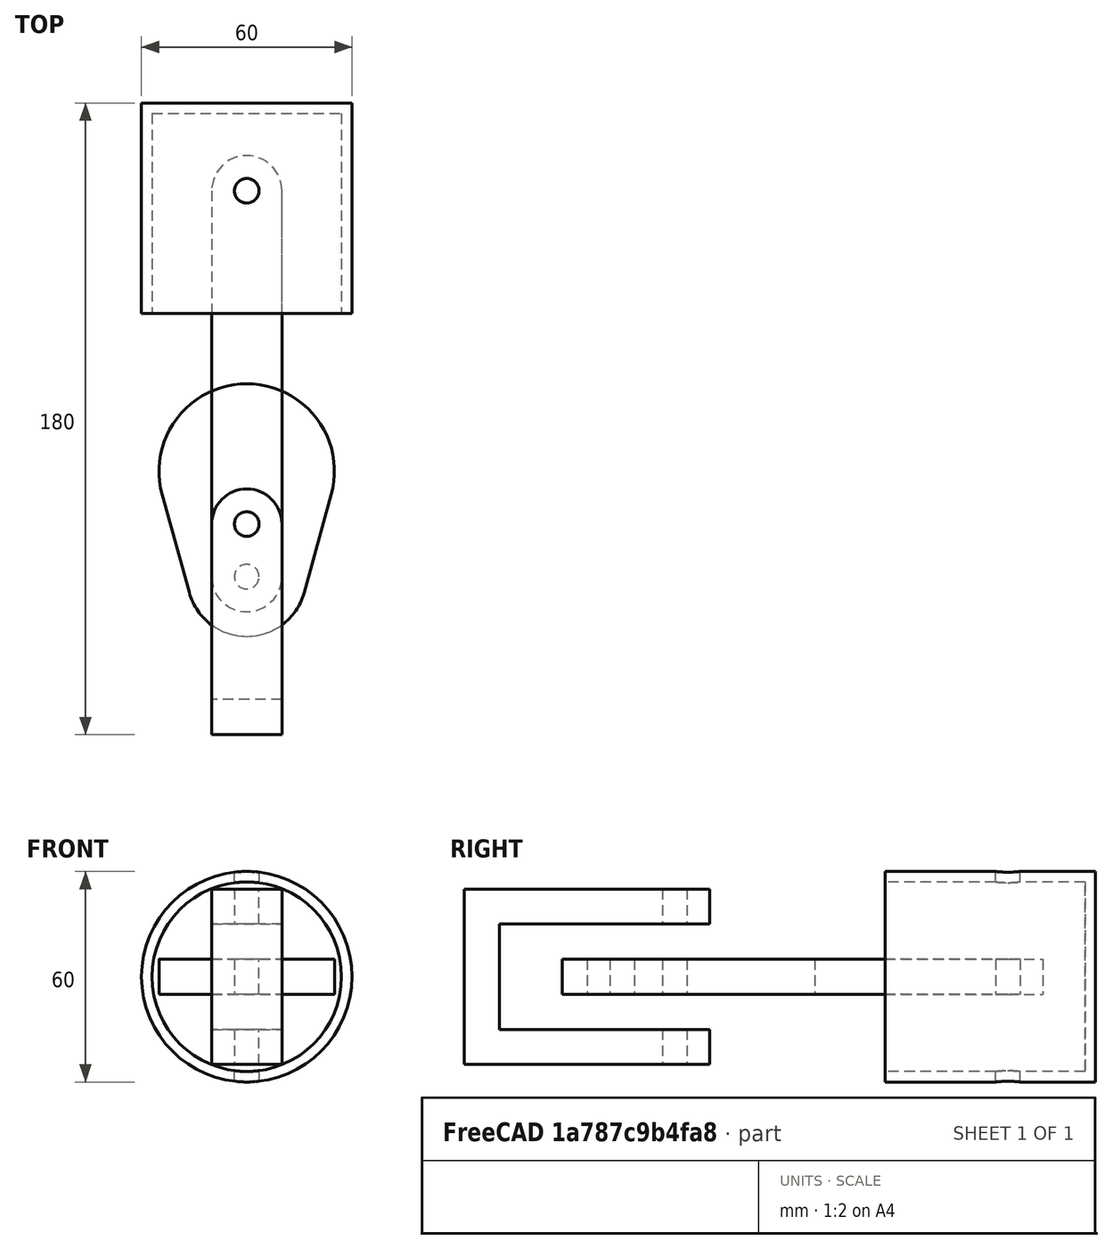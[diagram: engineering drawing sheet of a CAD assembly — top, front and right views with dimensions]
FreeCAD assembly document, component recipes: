
FREECAD ASSEMBLY — COMPONENT RECIPES ("Piston Head Assembly")

This assembly document has 5 components, labeled P0..P4 below (a component is one placed body or linked part). 5 of them carry a construction recipe — the FreeCAD feature program that regenerates the part from scratch, quoted from this document or its linked companion documents; the rest are supplied as boundary geometry only. No exploded tour is included for this assembly.
COMPONENT P0 — recipe-attached ("Crank001", modeled in this document).
Construction recipe (the document's own serialized feature program — sketch geometry with constraints, then the solid features built on it; lengths are millimeters unless a unit is written):

FEATURE [PartDesign::SubShapeBinder] Binder002
  BindCopyOnChange = 0
  BindMode = 0
  ClaimChildren = false
  Context = -> Body002 [Binder002.]
  Fuse = false
  MakeFace = false
  OffsetFill = false
  OffsetIntersection = false
  OffsetJoinType = 0
  OffsetOpenResult = false
  PartialLoad = false
  Refine = true
  Relative = true
  Support = -> [Sketch]
  _Version = 2
FEATURE [Sketcher::SketchObject] Sketch003
  ArcFitTolerance = 1e-06
  AttachmentSupport = -> [XY_Plane002]
  ExternalGeometry = -> [Binder002]
  FullyConstrained = true
  MakeInternals = false
  MapMode = 5
  sketch-geometry (6):
    g0: LineSegment StartX=-24.0947 StartY=-31.6667 StartZ=0 EndX=-16.3844 EndY=-59.5333 EndZ=0
    g1: ArcOfCircle CenterX=0 CenterY=-55 CenterZ=0 NormalX=0 NormalY=0 NormalZ=1 AngleXU=0 Radius=17 StartAngle=3.41153 EndAngle=6.01325
    g2: LineSegment StartX=16.3844 StartY=-59.5333 StartZ=0 EndX=24.0947 EndY=-31.6667 EndZ=0
    g3: ArcOfCircle CenterX=-1.6e-15 CenterY=-25 CenterZ=0 NormalX=0 NormalY=0 NormalZ=1 AngleXU=0 Radius=25 StartAngle=6.01325 EndAngle=9.69471
    g4: Circle CenterX=0 CenterY=-40 CenterZ=0 NormalX=0 NormalY=0 NormalZ=1 AngleXU=0 Radius=3.5
    g5: Circle CenterX=0 CenterY=-55 CenterZ=0 NormalX=0 NormalY=0 NormalZ=1 AngleXU=0 Radius=3.5
  constraints (12):
    c: Coincident(g-4,g0)
    c: Tangent(g0,g1) = -1.5708
    c: Coincident(g1,g-6)
    c: Coincident(g1,g2)
    c: Coincident(g2,g-6)
    c: Tangent(g2,g3) = -1.5708
    c: Coincident(g3,g0)
    c: Coincident(g0,g-5)
    c: Coincident(g4,g-7)
    c: Equal(g4,g-7)
    c: Coincident(g5,g1)
    c: Equal(g5,g-8)
FEATURE [PartDesign::Pad] Pad001
  Direction = (0,0,1)
  Length = 10
  Length2 = 10
  Midplane = true
  Profile = -> Sketch003
  ReferenceAxis = -> Sketch003 [N_Axis]
  Refine = true
  Suppressed = false
  Type = 0
FEATURE [PartDesign::Body] Body002  label="Crank"
  AllowCompound = false
  Group = -> [Binder002,Sketch003,Pad001]
  Origin = -> Origin002
  Tip = -> Pad001
COMPONENT P1 — same part as P0; its construction recipe is shown at P0.
COMPONENT P2 — recipe-attached ("Link001", modeled in this document).
Construction recipe (the document's own serialized feature program — sketch geometry with constraints, then the solid features built on it; lengths are millimeters unless a unit is written):

FEATURE [PartDesign::SubShapeBinder] Binder
  BindCopyOnChange = 0
  BindMode = 0
  ClaimChildren = false
  Context = -> Body [Binder.]
  Fuse = false
  MakeFace = false
  OffsetFill = false
  OffsetIntersection = false
  OffsetJoinType = 0
  OffsetOpenResult = false
  PartialLoad = false
  Refine = true
  Relative = true
  Support = -> [Sketch]
  _Version = 2
FEATURE [Sketcher::SketchObject] Sketch001
  ArcFitTolerance = 1e-06
  AttachmentSupport = -> [XY_Plane]
  ExternalGeometry = -> [Binder]
  FullyConstrained = true
  MakeInternals = false
  MapMode = 5
  sketch-geometry (6):
    g0: LineSegment StartX=-10 StartY=55 StartZ=0 EndX=-10 EndY=-55 EndZ=0
    g1: ArcOfCircle CenterX=3e-16 CenterY=-55 CenterZ=0 NormalX=0 NormalY=0 NormalZ=1 AngleXU=0 Radius=10 StartAngle=3.14159 EndAngle=6.28319
    g2: LineSegment StartX=10 StartY=-55 StartZ=0 EndX=10 EndY=55 EndZ=0
    g3: ArcOfCircle CenterX=-4e-16 CenterY=55 CenterZ=0 NormalX=0 NormalY=0 NormalZ=1 AngleXU=0 Radius=10 StartAngle=0 EndAngle=3.14159
    g4: Circle CenterX=3e-16 CenterY=-55 CenterZ=0 NormalX=0 NormalY=0 NormalZ=1 AngleXU=0 Radius=3.5
    g5: Circle CenterX=-4e-16 CenterY=55 CenterZ=0 NormalX=0 NormalY=0 NormalZ=1 AngleXU=0 Radius=3.5
  constraints (12):
    c: Coincident(g-4,g0)
    c: Coincident(g0,g-6)
    c: Tangent(g0,g1) = -1.5708
    c: Coincident(g1,g-6)
    c: Coincident(g1,g2)
    c: Coincident(g2,g-5)
    c: Tangent(g2,g3) = -1.5708
    c: Coincident(g3,g0)
    c: Coincident(g4,g1)
    c: Equal(g4,g-7)
    c: Coincident(g5,g3)
    c: Equal(g5,g-8)
FEATURE [PartDesign::Pad] Pad
  Direction = (0,0,1)
  Length = 10
  Length2 = 10
  Midplane = true
  Profile = -> Sketch001
  ReferenceAxis = -> Sketch001 [N_Axis]
  Refine = true
  Suppressed = false
  Type = 0
FEATURE [PartDesign::Body] Body  label="Link"
  AllowCompound = false
  Group = -> [Binder,Sketch001,Pad]
  Origin = -> Origin
  Tip = -> Pad
COMPONENT P3 — recipe-attached ("Mount001", modeled in this document).
Construction recipe (the document's own serialized feature program — sketch geometry with constraints, then the solid features built on it; lengths are millimeters unless a unit is written):

FEATURE [PartDesign::SubShapeBinder] Binder003
  BindCopyOnChange = 0
  BindMode = 0
  ClaimChildren = false
  Context = -> Body003 [Binder003.]
  Fuse = false
  MakeFace = false
  OffsetFill = false
  OffsetIntersection = false
  OffsetJoinType = 0
  OffsetOpenResult = false
  PartialLoad = false
  Refine = true
  Relative = true
  Support = -> [Sketch]
  _Version = 2
FEATURE [Sketcher::SketchObject] Sketch005
  ArcFitTolerance = 1e-06
  AttachmentSupport = -> [XY_Plane003]
  ExternalGeometry = -> [Binder003]
  FullyConstrained = true
  MakeInternals = false
  MapMode = 5
  sketch-geometry (5):
    g0: LineSegment StartX=-10 StartY=-40 StartZ=0 EndX=-10 EndY=-100 EndZ=0
    g1: LineSegment StartX=-10 StartY=-100 StartZ=0 EndX=10 EndY=-100 EndZ=0
    g2: LineSegment StartX=10 StartY=-100 StartZ=0 EndX=10 EndY=-40 EndZ=0
    g3: ArcOfCircle CenterX=1.8e-15 CenterY=-40 CenterZ=0 NormalX=0 NormalY=0 NormalZ=1 AngleXU=0 Radius=10 StartAngle=1e-16 EndAngle=3.14159
    g4: Circle CenterX=1.8e-15 CenterY=-40 CenterZ=0 NormalX=0 NormalY=0 NormalZ=1 AngleXU=0 Radius=3.5
  constraints (10):
    c: Tangent(g-4,g0) = -1.5708
    c: Coincident(g0,g1)
    c: Coincident(g1,g-6)
    c: Horizontal(g1)
    c: Coincident(g1,g2)
    c: Coincident(g2,g-5)
    c: Tangent(g2,g3) = -1.5708
    c: Coincident(g3,g0)
    c: Coincident(g4,g3)
    c: Equal(g4,g-7)
FEATURE [PartDesign::Pad] Pad002
  Direction = (0,0,1)
  Length = 50
  Length2 = 10
  Midplane = true
  Profile = -> Sketch005
  ReferenceAxis = -> Sketch005 [N_Axis]
  Refine = true
  Suppressed = false
  Type = 0
FEATURE [Sketcher::SketchObject] Sketch006
  ArcFitTolerance = 1e-06
  AttachmentSupport = -> [YZ_Plane003]
  ExternalGeometry = -> [Pad002]
  FullyConstrained = false
  MakeInternals = false
  MapMode = 5
  Placement = pos=(0,0,0) rot=(0.57735,0.57735,0.57735;2.0944rad)
  sketch-geometry (4):
    g0: LineSegment StartX=-90 StartY=15 StartZ=0 EndX=-90 EndY=-15 EndZ=0
    g1: LineSegment StartX=-90 StartY=-15 StartZ=0 EndX=-12.8642 EndY=-15 EndZ=0
    g2: LineSegment StartX=-12.8642 StartY=-15 StartZ=0 EndX=-12.8642 EndY=15 EndZ=0
    g3: LineSegment StartX=-12.8642 StartY=15 StartZ=0 EndX=-90 EndY=15 EndZ=0
  constraints (10):
    c: Coincident(g0,g1)
    c: Coincident(g1,g2)
    c: Coincident(g2,g3)
    c: Coincident(g3,g0)
    c: Vertical(g2)
    c: Horizontal(g1)
    c: Horizontal(g3)
    c: Symmetric(g0,g0,g-1)
    c: Distance(g1,g3) = 30
    c: Distance(g-3,g0) = 10
FEATURE [PartDesign::Pocket] Pocket001
  BaseFeature = -> Pad002
  Direction = (-1,0,0)
  Length = 30
  Length2 = 5
  Midplane = true
  Profile = -> Sketch006
  ReferenceAxis = -> Sketch006 [N_Axis]
  Refine = true
  Suppressed = false
  Type = 0
FEATURE [PartDesign::Body] Body003  label="Mount"
  AllowCompound = false
  Group = -> [Sketch005,Binder003,Pad002,Sketch006,Pocket001]
  Origin = -> Origin003
  Tip = -> Pocket001
COMPONENT P4 — recipe-attached ("Piston Head001", modeled in this document).
Construction recipe (the document's own serialized feature program — sketch geometry with constraints, then the solid features built on it; lengths are millimeters unless a unit is written):

FEATURE [PartDesign::SubShapeBinder] Binder001
  BindCopyOnChange = 0
  BindMode = 0
  ClaimChildren = false
  Context = -> Body001 [Binder001.]
  Fuse = false
  MakeFace = false
  OffsetFill = false
  OffsetIntersection = false
  OffsetJoinType = 0
  OffsetOpenResult = false
  PartialLoad = false
  Refine = true
  Relative = true
  Support = -> [Sketch]
  _Version = 2
FEATURE [Sketcher::SketchObject] Sketch002
  ArcFitTolerance = 1e-06
  AttachmentSupport = -> [XY_Plane001]
  ExternalGeometry = -> [Binder001]
  FullyConstrained = true
  MakeInternals = false
  MapMode = 5
  sketch-geometry (6):
    g0: LineSegment StartX=-30 StartY=20 StartZ=0 EndX=-30 EndY=80 EndZ=0
    g1: LineSegment StartX=-30 StartY=80 StartZ=0 EndX=0 EndY=80 EndZ=0
    g2: LineSegment StartX=0 StartY=80 StartZ=0 EndX=0 EndY=77 EndZ=0
    g3: LineSegment StartX=0 StartY=77 StartZ=0 EndX=-27 EndY=77 EndZ=0
    g4: LineSegment StartX=-27 StartY=77 StartZ=0 EndX=-27 EndY=20 EndZ=0
    g5: LineSegment StartX=-27 StartY=20 StartZ=0 EndX=-30 EndY=20 EndZ=0
  constraints (15):
    c: Coincident(g-6,g0)
    c: Coincident(g0,g-4)
    c: Coincident(g0,g1)
    c: Symmetric(g-4,g-4,g1)
    c: Coincident(g1,g2)
    c: PointOnObject(g2,g-2)
    c: Coincident(g2,g3)
    c: Horizontal(g3)
    c: Coincident(g3,g4)
    c: PointOnObject(g4,g-6)
    c: Vertical(g4)
    c: Coincident(g4,g5)
    c: Coincident(g5,g0)
    c: DistanceX(g5,g5) = 3
    c: DistanceY(g2,g2) = 3
FEATURE [PartDesign::Revolution] Revolution
  Angle = 360
  Angle2 = 60
  Axis = (0,1,0)
  Base = (0,0,0)
  Profile = -> Sketch002
  ReferenceAxis = -> Sketch002 [V_Axis]
  Refine = true
  Suppressed = false
  Type = 0
FEATURE [Sketcher::SketchObject] Sketch004
  ArcFitTolerance = 1e-06
  AttachmentSupport = -> [XY_Plane001]
  ExternalGeometry = -> [Binder001]
  FullyConstrained = true
  MakeInternals = false
  MapMode = 5
  sketch-geometry (1):
    g0: Circle CenterX=0 CenterY=55 CenterZ=0 NormalX=0 NormalY=0 NormalZ=1 AngleXU=0 Radius=3.5
  constraints (2):
    c: Coincident(g0,g-3)
    c: Equal(g0,g-3)
FEATURE [PartDesign::Pocket] Pocket
  BaseFeature = -> Revolution
  Direction = (0,0,-1)
  Length = 5
  Length2 = 5
  Midplane = true
  Profile = -> Sketch004
  ReferenceAxis = -> Sketch004 [N_Axis]
  Refine = true
  Suppressed = false
  Type = 1
FEATURE [PartDesign::Body] Body001  label="Piston Head"
  AllowCompound = false
  Group = -> [Binder001,Sketch002,Revolution,Sketch004,Pocket]
  Origin = -> Origin001
  Tip = -> Pocket
PROVENANCE & LICENSES
A FreeCAD (.FCStd) document from a public repository crawl; recipes are the document's own serialized feature recipes (and, for linked parts, companion documents' recipes).
License: as declared in the source repository (recorded in the dataset sidecar).
